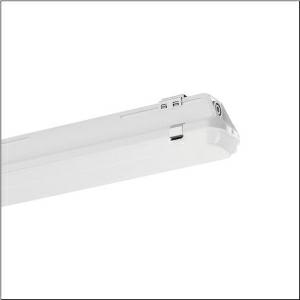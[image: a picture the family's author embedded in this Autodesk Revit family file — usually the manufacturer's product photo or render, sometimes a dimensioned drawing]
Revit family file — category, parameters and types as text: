
# Revit family: monsun_r__21_51fb107l440k005_010f
name_source: partatom
category: Lighting Fixtures
units: mm (PartAtom-declared; Revit-internal decimal feet)

## family parameters
Cut with Voids When Loaded = No
Host = Face
Light Source = No
Part Type = Normal
Room Calculation Point = No
Round Connector Dimension = Use Diameter
Shared = No

## types (1)
- Monsun® 21 (1 x LED, 4350 lm, 24.7 W, 4000K)
    Apparent Load = 25 VA
    CIE Flux Codes = 46 76 93 94 100
    Color Rendering = 80
    Color Temperature = 4000K
    Default Elevation = 1800 mm
    Description = Monsun® 21, damp-proof luminaire, chain hanger, primary optical cover: enclosure, of PMMA, light emission: direct distribution, primary light characteristic: symmetric, installation type: vertical mounting, horizontal mounting, surface-mounted, suspended mounting, LED, rated luminous flux: 4.350lm, luminous efficacy: 176lm/W, light colour: 840, colour temperature: 4000K, control gear: ON/OFF, with terminal, 3-pole, max. 2.5mm², through-wiring: 5x 2.5mm², mains connection: 220..240V, AC, 50/60Hz, rated input power: 25W, housing, of glass-fibre reinforced plastic, uncoated, bright grey, incl. chain hanger, length: 1.299mm, width: 90mm, height: 88mm, clip for enclosure, of stainless steel (V2A), ceiling mounting element, of stainless steel (V2A), chain hanger, of stainless steel (V2A), protection rating (complete): IP66, insulation class (complete): insulation class I (protective earthing), certification: CE, ENEC, VDE, UKCA, protection symbol: D, impact resistance: IK04, permissible operating ambient temperature: -25..+35°C, standard: EN 50419, EN 60598-2-1, corresponds to IFS (International Featured Standards) requirements for safety and quality in the food industry, for indoor or canopied outdoor use, no direct snow, no direct sun, no direct rain, LABS conformity tested according to VDMA 24364:2018-05, contact your sales advisor before using the luminaires in applications with unclear chemical exposure, large temperature fluctuations or condensation-forming humidity, packaging unit: 1 piece
    Height = 88 mm
    Lamp = 1 x LED
    Lamp Light Flux = 4350 lm
    Lamp Power = 24.7 W
    Lamp count = 1
    Length = 1299 mm
    Luminous efficacy = 176 lm/W
    Manufacturer = Siteco
    ModVariant = No
    Model = 51FB107L440K005
    Mounting Place = Ceiling
    Mounting Type = Surface mounted
    Number of Poles = 1
    OnlyDefault = Yes
    Power Factor = 1
    Product Name = Monsun® 21
    Product group = damp-proof luminaire
    ProductGroupID = 300
    Protection Class = Protection class I
    Protection Degree = IP 66
    RLX_Detail_Level = 1
    RLX_Emergency_Light_Flux = 0 lm
    RLX_Emergency_Type = 0
    RLX_Emergency_Type_DB = No
    RlxData = <blob elided: 89881 chars, md5=9222b42d>
    Socket = socket
    Standby Power = 0 W
    System Light Flux = 4350 lm
    System Power = 25 W
    Type Comments = Product without accessories
    Type Image = l_1319656.jpg
    URL = http://relux.com
    VarID = ---
    Voltage = 0 V
    Weight = 0.00 kg
    Width = 90 mm

## geometry (parser evidence)
native form markers: Blend x4, Sweep x14
no freeform markers — native parametric forms only
